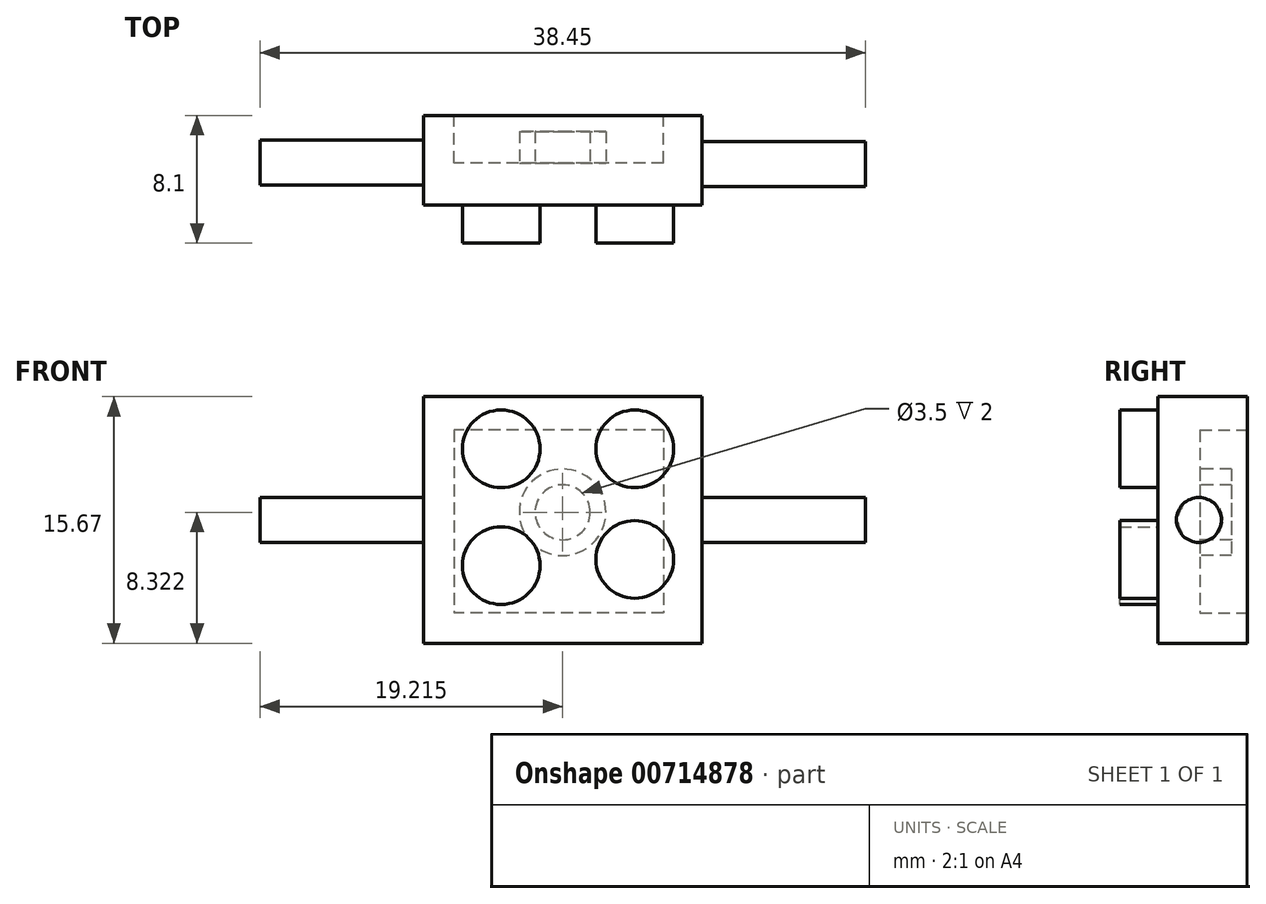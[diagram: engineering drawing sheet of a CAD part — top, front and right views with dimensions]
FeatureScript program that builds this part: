
annotation { "Feature Type Name" : "Feature", "Feature Type Description" : "" }
export const myFeature = defineFeature(function(context is Context, id is Id, definition is map)
    precondition{}
    {
        {
            var Q0;
            Q0=qCreatedBy(makeId("Front.planeOp"),FACE);
            var sketch = newSketch(context, id + "F0", { "sketchPlane" : qUnion([Q0])});
            skCircle(sketch, "E0", {"center": v(-31.02, 13.5) * mm, "radius": 7.84 * mm});
            skCircle(sketch, "E1", {"center": v(27.66, 13.5) * mm, "radius": 7.78 * mm});
            skCircle(sketch, "E2", {"center": v(-31.02, -35.79) * mm, "radius": 7.78 * mm});
            skCircle(sketch, "E3", {"center": v(27.66, -35.79) * mm, "radius": 7.78 * mm});
            skSolve(sketch);
        }
        {
            var Q0;
            Q0=qSketchRegion(id+"F0",true);
            extrude(context, id + "F1", {"entities" : qUnion([Q0]), "depth" : 5.67 * mm, "offsetDistance" : 25 * mm});
        }
        {
            var Q0;
            Q0=qCreatedBy(makeId("Front.planeOp"),FACE);
            var sketch = newSketch(context, id + "F2", { "sketchPlane" : qUnion([Q0])});
            skLineSegment(sketch, "E4", {"start": v(-84.9, 44.94) * mm, "end": v(-67.21, 44.94) * mm});
            skLineSegment(sketch, "E5", {"start": v(-84.9, 29.27) * mm, "end": v(-67.21, 29.27) * mm});
            skPoint(sketch, "E6.start.orphan", {"position": v(-67.21, 39.5) * mm});
            skPoint(sketch, "E7.end.orphan", {"position": v(-84.9, 35.35) * mm});
            skLineSegment(sketch, "E8", {"start": v(-84.9, 44.94) * mm, "end": v(-84.9, 29.27) * mm});
            skLineSegment(sketch, "E9", {"start": v(-67.21, 44.94) * mm, "end": v(-67.21, 29.27) * mm});
            skSolve(sketch);
        }
        {
            var Q0;
            Q0=qSketchRegion(id+"F2",true);
            extrude(context, id + "F3", {"entities" : qUnion([Q0]), "depth" : 5.67 * mm, "offsetDistance" : 25 * mm});
        }
        {
            var Q0;
            Q0=makeQuery(id+"F3.opExtrude","SWEPT_FACE",FACE,{"disambiguationData":[OSD([sQuery(id+"F2.wireOp",EDGE,"E8")])]});
            var sketch = newSketch(context, id + "F4", { "sketchPlane" : qUnion([Q0])});
            skPoint(sketch, "E10.centerSnap0", {"position": v(0, 37.1) * mm});
            skCircle(sketch, "E11", {"center": v(2.97, 37.1) * mm, "radius": 1.43 * mm});
            skSolve(sketch);
        }
        {
            var Q0;
            Q0=qSketchRegion(id+"F4",true);
            extrude(context, id + "F5", {"entities" : qUnion([Q0]), "operationType" : NewBodyOperationType.ADD, "depth" : 10.38 * mm, "offsetDistance" : 25 * mm});
        }
        {
            var Q0;
            Q0=makeQuery(id+"F3.opExtrude","SWEPT_FACE",FACE,{"disambiguationData":[OSD([sQuery(id+"F2.wireOp",EDGE,"E9")])]});
            var sketch = newSketch(context, id + "F6", { "sketchPlane" : qUnion([Q0])});
            skCircle(sketch, "E12", {"center": v(-3.07, 37.1) * mm, "radius": 1.43 * mm});
            skPoint(sketch, "E12.centerSnap0", {"position": v(0, 37.1) * mm});
            skSolve(sketch);
        }
        {
            var Q0;
            Q0=qSketchRegion(id+"F6",true);
            extrude(context, id + "F7", {"entities" : qUnion([Q0]), "operationType" : NewBodyOperationType.ADD, "depth" : 10.38 * mm, "offsetDistance" : 25 * mm});
        }
        {
            var Q0;
            Q0=makeQuery(id+"F1.opExtrude","SWEPT_BODY",BODY,{"disambiguationData":[OSD([sQuery(id+"F0.wireOp",EDGE,"E1")])]});
            var Q1;
            Q1=makeQuery(id+"F1.opExtrude","SWEPT_BODY",BODY,{"disambiguationData":[OSD([sQuery(id+"F0.wireOp",EDGE,"E0")])]});
            var Q2;
            Q2=makeQuery(id+"F1.opExtrude","SWEPT_BODY",BODY,{"disambiguationData":[OSD([sQuery(id+"F0.wireOp",EDGE,"E2")])]});
            var Q3;
            Q3=makeQuery(id+"F1.opExtrude","SWEPT_BODY",BODY,{"disambiguationData":[OSD([sQuery(id+"F0.wireOp",EDGE,"E3")])]});
            deleteBodies(context, id + "F8", {"entities" : qUnion([Q0, Q1, Q2, Q3])});
        }
        {
            var Q0;
            Q0=makeQuery(id+"F3.opExtrude","CAP_FACE",FACE,{"disambiguationData":[OSD([sQuery(id+"F2.wireOp",EDGE,"E4"),sQuery(id+"F2.wireOp",EDGE,"E5"),sQuery(id+"F2.wireOp",EDGE,"E8"),sQuery(id+"F2.wireOp",EDGE,"E9")])],"isStart":false});
            var sketch = newSketch(context, id + "F9", { "sketchPlane" : qUnion([Q0])});
            skCircle(sketch, "E13", {"center": v(-79.96, 41.62) * mm, "radius": 2.46 * mm});
            skCircle(sketch, "E14", {"center": v(-71.48, 41.62) * mm, "radius": 2.46 * mm});
            skCircle(sketch, "E15", {"center": v(-79.96, 34.2) * mm, "radius": 2.46 * mm});
            skCircle(sketch, "E16", {"center": v(-71.48, 34.6) * mm, "radius": 2.46 * mm});
            skSolve(sketch);
        }
        {
            var Q0;
            Q0 = qSketchRegion(id + "F9", true);
            extrude(context, id + "F10", {"entities" : qUnion([Q0]), "operationType" : NewBodyOperationType.ADD, "depth" : 2.42 * mm, "offsetDistance" : 25 * mm});
        }
        {
            var Q0;
            Q0=makeQuery(id+"F3.opExtrude","CAP_FACE",FACE,{"disambiguationData":[OSD([sQuery(id+"F2.wireOp",EDGE,"E4"),sQuery(id+"F2.wireOp",EDGE,"E5"),sQuery(id+"F2.wireOp",EDGE,"E8"),sQuery(id+"F2.wireOp",EDGE,"E9")])],"isStart":true});
            var sketch = newSketch(context, id + "F11", { "sketchPlane" : qUnion([Q0])});
            skLineSegment(sketch, "E17.bottom", {"start": v(69.66, 42.81) * mm, "end": v(82.97, 42.81) * mm});
            skLineSegment(sketch, "E17.top", {"start": v(69.66, 31.2) * mm, "end": v(82.97, 31.2) * mm});
            skLineSegment(sketch, "E17.left", {"start": v(69.66, 42.81) * mm, "end": v(69.66, 31.2) * mm});
            skLineSegment(sketch, "E17.right", {"start": v(82.97, 42.81) * mm, "end": v(82.97, 31.2) * mm});
            skSolve(sketch);
        }
        {
            var Q0;
            Q0 = qSketchRegion(id + "F11", true);
            extrude(context, id + "F12", {"entities" : qUnion([Q0]), "operationType" : NewBodyOperationType.REMOVE, "oppositeDirection" : true, "depth" : 3 * mm, "offsetDistance" : 25 * mm});
        }
        {
            var Q0;
            Q0=makeQuery(id+"F12.boolean.opBoolean","COPY",FACE,{"derivedFrom":makeQuery(id+"F12.opExtrude","CAP_FACE",FACE,{"disambiguationData":[OSD([sQuery(id+"F11.wireOp",EDGE,"E17.bottom"),sQuery(id+"F11.wireOp",EDGE,"E17.top"),sQuery(id+"F11.wireOp",EDGE,"E17.left"),sQuery(id+"F11.wireOp",EDGE,"E17.right")])],"isStart":false})});
            var sketch = newSketch(context, id + "F13", { "sketchPlane" : qUnion([Q0])});
            skCircle(sketch, "E18", {"center": v(76.07, 37.6) * mm, "radius": 2.75 * mm});
            skCircle(sketch, "E19", {"center": v(76.07, 37.6) * mm, "radius": 1.75 * mm});
            skSolve(sketch);
        }
        {
            var Q0;
            Q0 = qSketchRegion(id + "F13", true);
            extrude(context, id + "F14", {"entities" : qUnion([Q0]), "operationType" : NewBodyOperationType.ADD, "depth" : 2 * mm, "offsetDistance" : 25 * mm});
        }
    });
